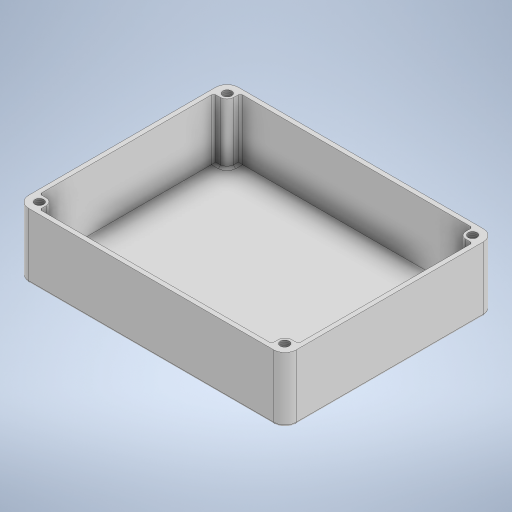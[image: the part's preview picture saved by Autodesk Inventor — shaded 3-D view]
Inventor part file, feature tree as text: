
AUTODESK INVENTOR PART (.ipt)
format: ipt  version: 2024 (Build 280153000, 153)  size: 370,176 bytes
history: native  units: mm
features: fillet x4, other x4, extrude x3, sketch x2, projected_geometry x1
ambient origin geometry x8: Origin, YZ Plane, XZ Plane, XY Plane, X Axis, Y Axis, Z Axis, Center Point
bodies: Solide1 (feature_tree)
feature tree (14):
  sketch  "Esquisse1"
  extrude  "Extrusion1"  Depth=120.0mm
  extrude  "Extrusion2"  Depth=94.0mm
  fillet  "Congé1"  Radius=8.0mm
  fillet  "Congé2"  Radius=8.0mm
  fillet  "Congé3"  Radius=8.0mm
  extrude  "Extrusion3"  Depth=8.0mm
  other  "Filetage1"
  other  "Filetage2"
  other  "Filetage3"
  other  "Filetage4"
  fillet  "Congé4"  Radius=8.0mm
  sketch  "Esquisse2"
  projected_geometry  "Boucle projetée1"
